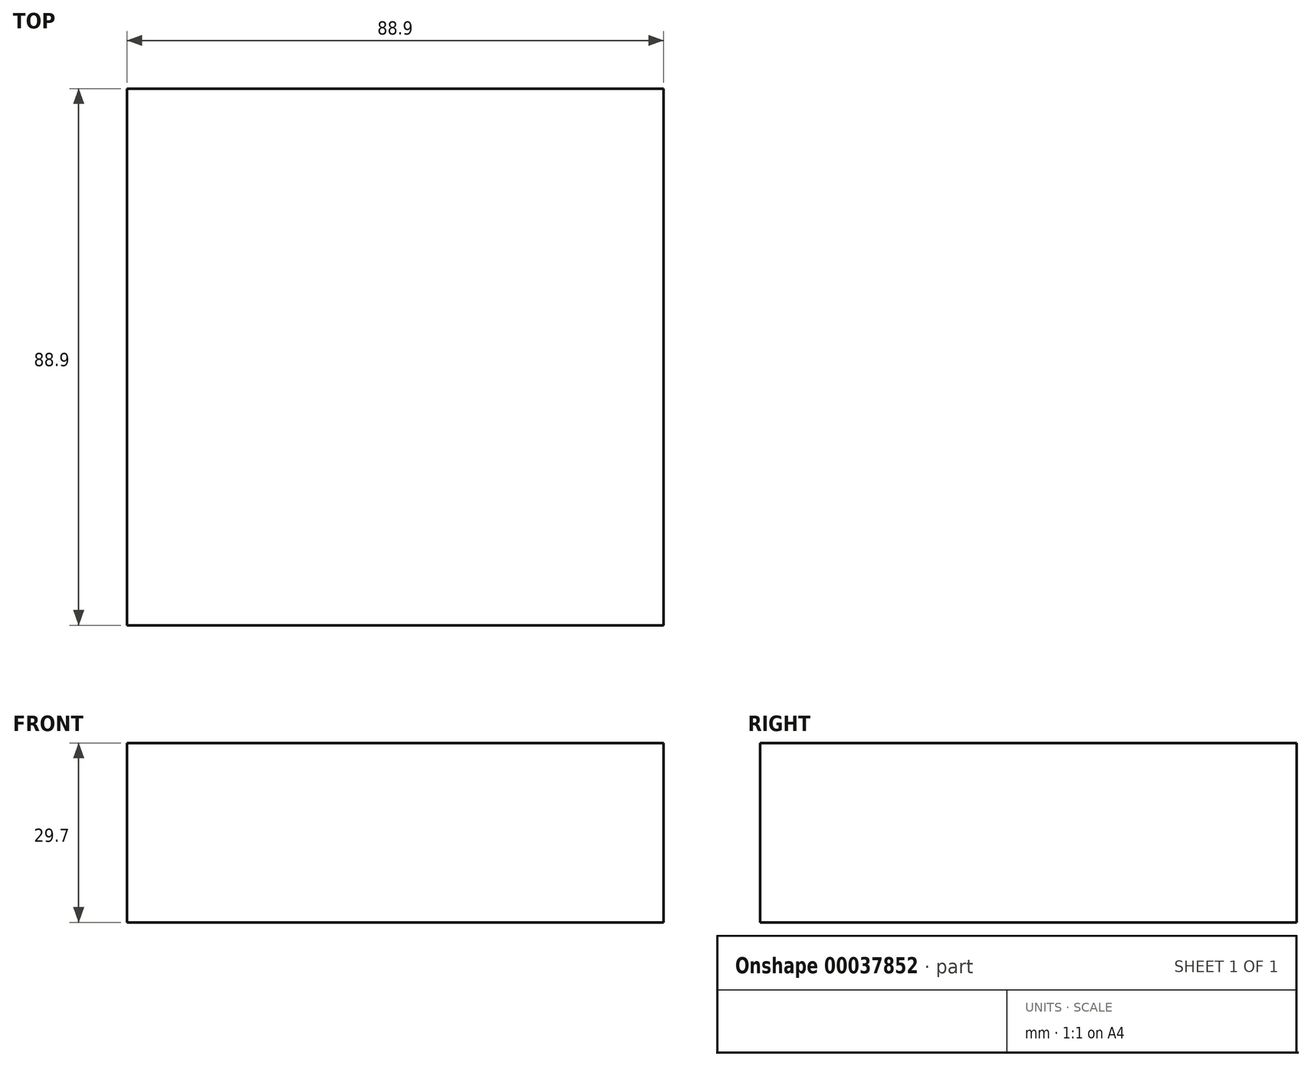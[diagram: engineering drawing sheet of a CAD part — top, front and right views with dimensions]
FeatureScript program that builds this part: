
annotation { "Feature Type Name" : "Feature", "Feature Type Description" : "" }
export const myFeature = defineFeature(function(context is Context, id is Id, definition is map)
    precondition{}
    {
        {
            var Q0;
            Q0=qCreatedBy(makeId("Top.planeOp"),FACE);
            var sketch = newSketch(context, id + "F0", { "sketchPlane" : qUnion([Q0])});
            skLineSegment(sketch, "E0.rect.bottom", {"start": v(-44.45, 44.45) * mm, "end": v(44.45, 44.45) * mm});
            skLineSegment(sketch, "E0.rect.top", {"start": v(-44.45, -44.45) * mm, "end": v(44.45, -44.45) * mm});
            skLineSegment(sketch, "E0.rect.left", {"start": v(-44.45, 44.45) * mm, "end": v(-44.45, -44.45) * mm});
            skLineSegment(sketch, "E0.rect.right", {"start": v(44.45, 44.45) * mm, "end": v(44.45, -44.45) * mm});
            skPoint(sketch, "E0.rect.middle", {"position": v(0, 0) * mm});
            skSolve(sketch);
        }
        {
            var Q0;
            Q0=makeQuery(id+"F0.imprint","IMPRINT",FACE,{"disambiguationData":[TD([[makeQuery(id+"F0.imprint","IMPRINT",EDGE,{"derivedFrom":sQuery(id+"F0.wireOp",EDGE,"E0.rect.bottom")}),-1.0]])]});
            extrude(context, id + "F1", {"entities" : qUnion([Q0]), "depth" : 29.7 * mm});
        }
    });
